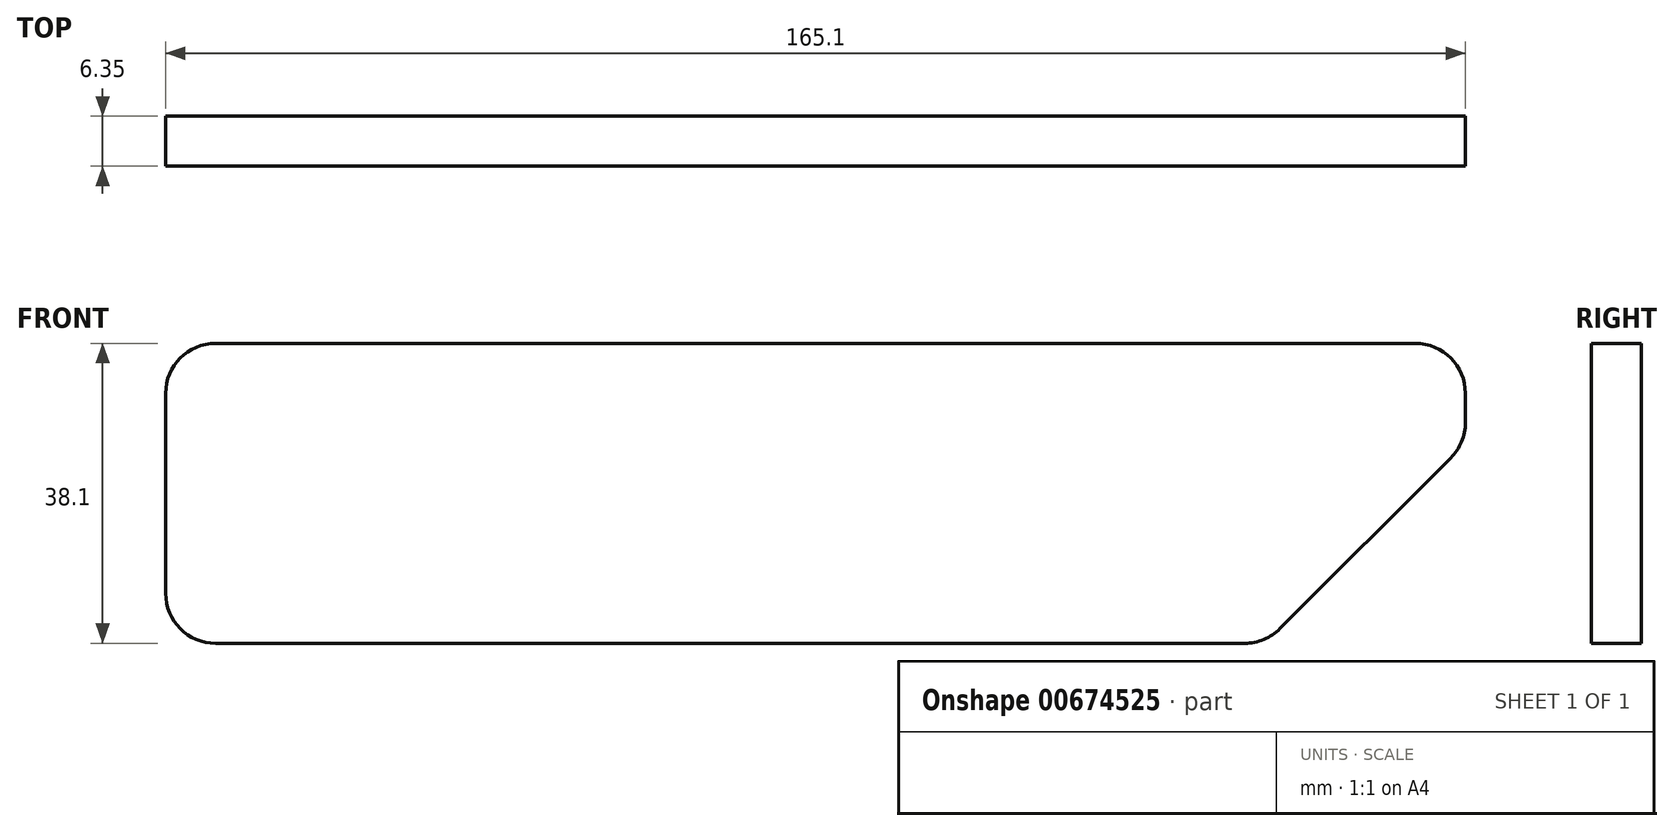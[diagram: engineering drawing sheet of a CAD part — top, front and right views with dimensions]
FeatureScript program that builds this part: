
annotation { "Feature Type Name" : "Feature", "Feature Type Description" : "" }
export const myFeature = defineFeature(function(context is Context, id is Id, definition is map)
    precondition{}
    {
        {
            var Q0;
            Q0=qCreatedBy(makeId("Front.planeOp"),FACE);
            var sketch = newSketch(context, id + "F0", { "sketchPlane" : qUnion([Q0])});
            skLineSegment(sketch, "E0.bottom", {"start": v(76.2, 19.05) * mm, "end": v(-76.2, 19.05) * mm});
            skLineSegment(sketch, "E0.top", {"start": v(54.52, -19.05) * mm, "end": v(-76.2, -19.05) * mm});
            skLineSegment(sketch, "E0.left", {"start": v(82.55, 12.7) * mm, "end": v(82.55, 8.98) * mm});
            skLineSegment(sketch, "E0.right", {"start": v(-82.55, 12.7) * mm, "end": v(-82.55, -12.7) * mm});
            skPoint(sketch, "E0.middle", {"position": v(0, 0) * mm});
            skLineSegment(sketch, "E1", {"start": v(59, -17.2) * mm, "end": v(80.7, 4.5) * mm});
            skPoint(sketch, "E2.start.orphan", {"position": v(82.55, -19.05) * mm});
            skPoint(sketch, "E3.visualSharp", {"position": v(82.55, 19.05) * mm});
            skArc(sketch, "E3.filletArc", {"start": v(82.55, 12.7) * mm, "mid": v(80.7, 17.2) * mm, "end": v(76.2, 19.05) * mm});
            skPoint(sketch, "E4.visualSharp", {"position": v(82.55, 6.35) * mm});
            skArc(sketch, "E4.filletArc", {"start": v(80.7, 4.5) * mm, "mid": v(82.07, 6.55) * mm, "end": v(82.55, 8.98) * mm});
            skPoint(sketch, "E5.visualSharp", {"position": v(57.15, -19.05) * mm});
            skArc(sketch, "E5.filletArc", {"start": v(54.52, -19.05) * mm, "mid": v(56.95, -18.57) * mm, "end": v(59, -17.2) * mm});
            skPoint(sketch, "E6.visualSharp", {"position": v(-82.55, -19.05) * mm});
            skArc(sketch, "E6.filletArc", {"start": v(-82.55, -12.7) * mm, "mid": v(-80.7, -17.2) * mm, "end": v(-76.2, -19.05) * mm});
            skPoint(sketch, "E7.visualSharp", {"position": v(-82.55, 19.05) * mm});
            skArc(sketch, "E7.filletArc", {"start": v(-76.2, 19.05) * mm, "mid": v(-80.7, 17.2) * mm, "end": v(-82.55, 12.7) * mm});
            skSolve(sketch);
        }
        {
            var Q0;
            Q0=makeQuery(id+"F0.imprint","IMPRINT",FACE,{"disambiguationData":[TD([[makeQuery(id+"F0.imprint","IMPRINT",EDGE,{"derivedFrom":sQuery(id+"F0.wireOp",EDGE,"E0.bottom")}),1.0]])]});
            extrude(context, id + "F1", {"entities" : qUnion([Q0]), "depth" : 6.35 * mm, "offsetDistance" : 25.4 * mm});
        }
    });
